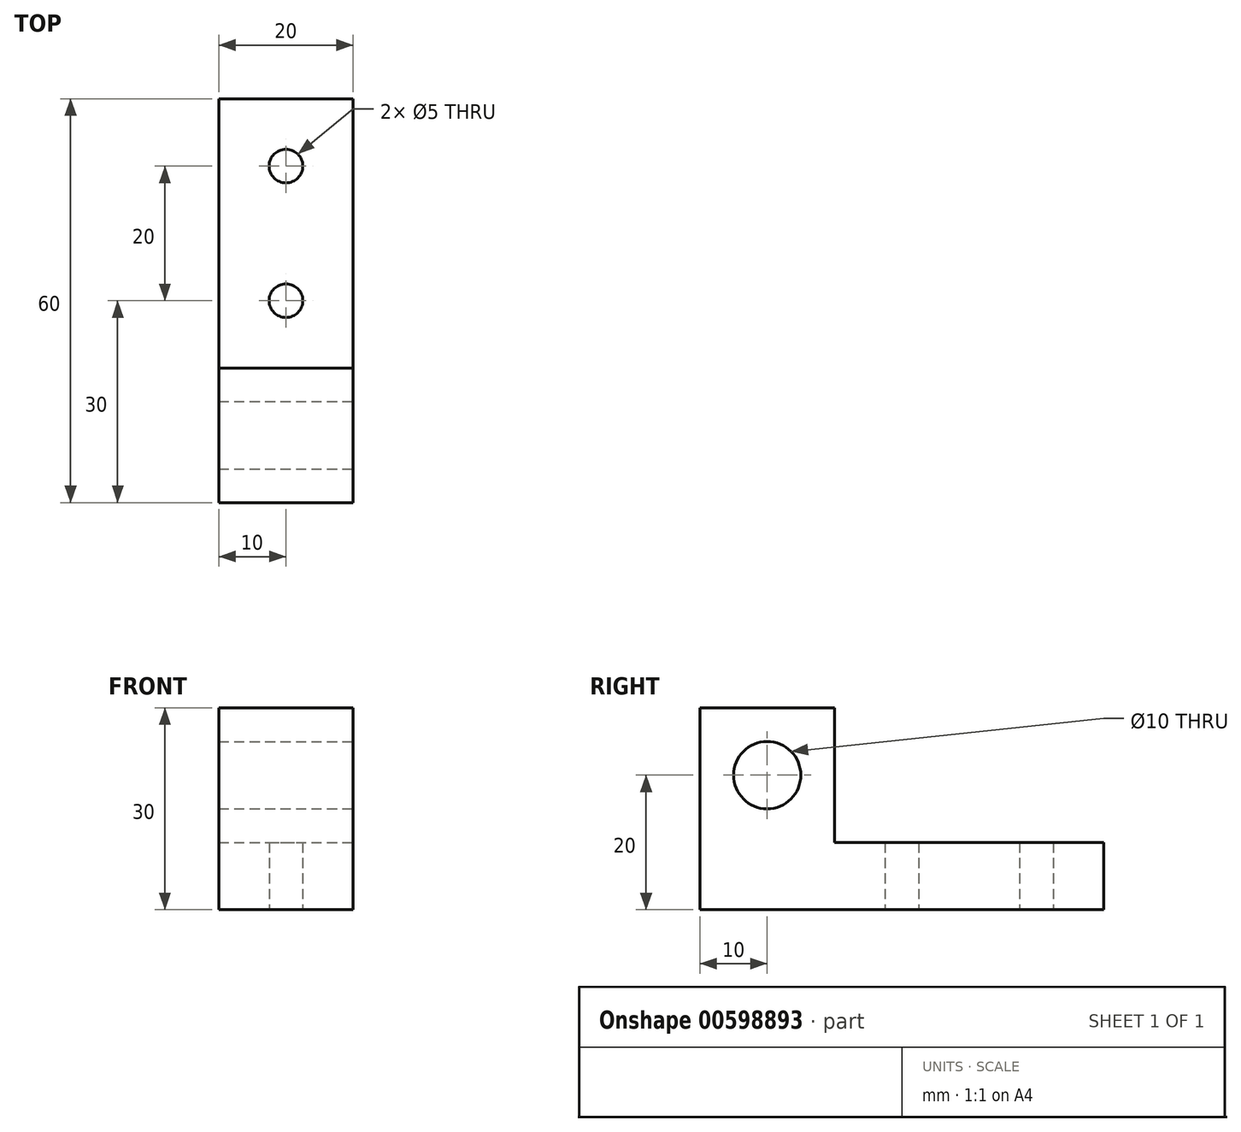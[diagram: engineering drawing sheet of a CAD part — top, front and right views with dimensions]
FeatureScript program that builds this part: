
annotation { "Feature Type Name" : "Feature", "Feature Type Description" : "" }
export const myFeature = defineFeature(function(context is Context, id is Id, definition is map)
    precondition{}
    {
        {
            var Q0;
            Q0=qCreatedBy(makeId("Top.planeOp"),FACE);
            var sketch = newSketch(context, id + "F0", { "sketchPlane" : qUnion([Q0])});
            skLineSegment(sketch, "E0.bottom", {"start": v(10, -30) * mm, "end": v(-10, -30) * mm});
            skLineSegment(sketch, "E0.top", {"start": v(10, 30) * mm, "end": v(-10, 30) * mm});
            skLineSegment(sketch, "E0.left", {"start": v(10, -30) * mm, "end": v(10, 30) * mm});
            skLineSegment(sketch, "E0.right", {"start": v(-10, -30) * mm, "end": v(-10, 30) * mm});
            skPoint(sketch, "E0.middle", {"position": v(0, 0) * mm});
            skSolve(sketch);
        }
        {
            var Q0;
            Q0=qSketchRegion(id+"F0",true);
            extrude(context, id + "F1", {"entities" : qUnion([Q0]), "depth" : 10 * mm, "offsetDistance" : 25 * mm});
        }
        {
            var Q0;
            Q0=makeQuery(id+"F1.opExtrude","CAP_FACE",FACE,{"disambiguationData":[OSD([sQuery(id+"F0.wireOp",EDGE,"E0.bottom"),sQuery(id+"F0.wireOp",EDGE,"E0.top"),sQuery(id+"F0.wireOp",EDGE,"E0.left"),sQuery(id+"F0.wireOp",EDGE,"E0.right")])],"isStart":false});
            var sketch = newSketch(context, id + "F2", { "sketchPlane" : qUnion([Q0])});
            skLineSegment(sketch, "E1", {"start": v(-10, -10) * mm, "end": v(10, -10) * mm});
            skLineSegment(sketch, "E2", {"start": v(-10, -10) * mm, "end": v(-10, -30) * mm});
            skLineSegment(sketch, "E3", {"start": v(-10, -30) * mm, "end": v(10, -30) * mm});
            skLineSegment(sketch, "E4", {"start": v(10, -30) * mm, "end": v(10, -10) * mm});
            skSolve(sketch);
        }
        {
            var Q0;
            Q0=makeQuery(id+"F2.imprint","IMPRINT",FACE,{"disambiguationData":[TD([[makeQuery(id+"F2.imprint","IMPRINT",EDGE,{"derivedFrom":sQuery(id+"F2.wireOp",EDGE,"E1")}),-1.0]])]});
            extrude(context, id + "F3", {"entities" : qUnion([Q0]), "operationType" : NewBodyOperationType.ADD, "depth" : 20 * mm, "offsetDistance" : 25 * mm});
        }
        {
            var Q0;
            Q0=makeQuery(id+"F1.opExtrude","CAP_FACE",FACE,{"disambiguationData":[OSD([sQuery(id+"F0.wireOp",EDGE,"E0.bottom"),sQuery(id+"F0.wireOp",EDGE,"E0.top"),sQuery(id+"F0.wireOp",EDGE,"E0.left"),sQuery(id+"F0.wireOp",EDGE,"E0.right")])],"isStart":false});
            var sketch = newSketch(context, id + "F4", { "sketchPlane" : qUnion([Q0])});
            skLineSegment(sketch, "E5", {"start": v(0, 30) * mm, "end": v(0, 1.46) * mm, "construction": true});
            skPoint(sketch, "E6", {"position": v(0, 20) * mm});
            skSolve(sketch);
        }
        {
            var Q0;
            Q0=sQuery(id+"F4.wireOp",VERTEX,"E6");
            var Q1;
            Q1=makeQuery(id+"F1.opExtrude","SWEPT_BODY",BODY,{"disambiguationData":[OSD([sQuery(id+"F0.wireOp",EDGE,"E0.bottom"),sQuery(id+"F0.wireOp",EDGE,"E0.top"),sQuery(id+"F0.wireOp",EDGE,"E0.left"),sQuery(id+"F0.wireOp",EDGE,"E0.right")])]});
            hole(context, id + "F5", {"style" : HoleStyle.SIMPLE, "endStyle" : HoleEndStyle.THROUGH, "holeDiameter" : 5 * mm, "majorDiameter" : 5 * mm, "isTappedThrough" : true, "tappedDepth" : 12 * mm, "tapClearance" : 3, "locations" : qUnion([Q0]), "scope" : qUnion([Q1])});
        }
        {
            var Q0;
            Q0=makeQuery(id+"F1.opExtrude","CAP_FACE",FACE,{"disambiguationData":[OSD([sQuery(id+"F0.wireOp",EDGE,"E0.bottom"),sQuery(id+"F0.wireOp",EDGE,"E0.top"),sQuery(id+"F0.wireOp",EDGE,"E0.left"),sQuery(id+"F0.wireOp",EDGE,"E0.right")])],"isStart":false});
            var sketch = newSketch(context, id + "F6", { "sketchPlane" : qUnion([Q0])});
            skLineSegment(sketch, "E7", {"start": v(0, 30) * mm, "end": v(0, 4.91) * mm});
            skPoint(sketch, "E7.endSnap0", {"position": v(0, 30) * mm});
            skPoint(sketch, "E8", {"position": v(0, 0) * mm});
            skSolve(sketch);
        }
        {
            var Q0;
            Q0=sQuery(id+"F6.wireOp",VERTEX,"E8");
            var Q1;
            Q1=makeQuery(id+"F1.opExtrude","SWEPT_BODY",BODY,{"disambiguationData":[OSD([sQuery(id+"F0.wireOp",EDGE,"E0.bottom"),sQuery(id+"F0.wireOp",EDGE,"E0.top"),sQuery(id+"F0.wireOp",EDGE,"E0.left"),sQuery(id+"F0.wireOp",EDGE,"E0.right")])]});
            hole(context, id + "F7", {"style" : HoleStyle.SIMPLE, "endStyle" : HoleEndStyle.THROUGH, "holeDiameter" : 5 * mm, "majorDiameter" : 5 * mm, "isTappedThrough" : true, "tappedDepth" : 12 * mm, "tapClearance" : 3, "locations" : qUnion([Q0]), "scope" : qUnion([Q1])});
        }
        {
            var Q0;
            Q0=makeQuery(id+"F3.boolean.opBoolean","MERGE",FACE,{"derivedFrom":[makeQuery(id+"F1.opExtrude","SWEPT_FACE",FACE,{"disambiguationData":[OSD([sQuery(id+"F0.wireOp",EDGE,"E0.right")])]}),makeQuery(id+"F3.opExtrude","SWEPT_FACE",FACE,{"disambiguationData":[OSD([sQuery(id+"F2.wireOp",EDGE,"E2")])]})]});
            var sketch = newSketch(context, id + "F8", { "sketchPlane" : qUnion([Q0])});
            skLineSegment(sketch, "E9", {"start": v(10, 20) * mm, "end": v(30, 20) * mm, "construction": true});
            skPoint(sketch, "E10", {"position": v(20, 20) * mm});
            skSolve(sketch);
        }
        {
            var Q0;
            Q0=sQuery(id+"F8.wireOp",VERTEX,"E10");
            var Q1;
            Q1=makeQuery(id+"F1.opExtrude","SWEPT_BODY",BODY,{"disambiguationData":[OSD([sQuery(id+"F0.wireOp",EDGE,"E0.bottom"),sQuery(id+"F0.wireOp",EDGE,"E0.top"),sQuery(id+"F0.wireOp",EDGE,"E0.left"),sQuery(id+"F0.wireOp",EDGE,"E0.right")])]});
            hole(context, id + "F9", {"style" : HoleStyle.SIMPLE, "endStyle" : HoleEndStyle.THROUGH, "holeDiameter" : 10 * mm, "majorDiameter" : 5 * mm, "isTappedThrough" : true, "tappedDepth" : 12 * mm, "tapClearance" : 3, "locations" : qUnion([Q0]), "scope" : qUnion([Q1])});
        }
    });
